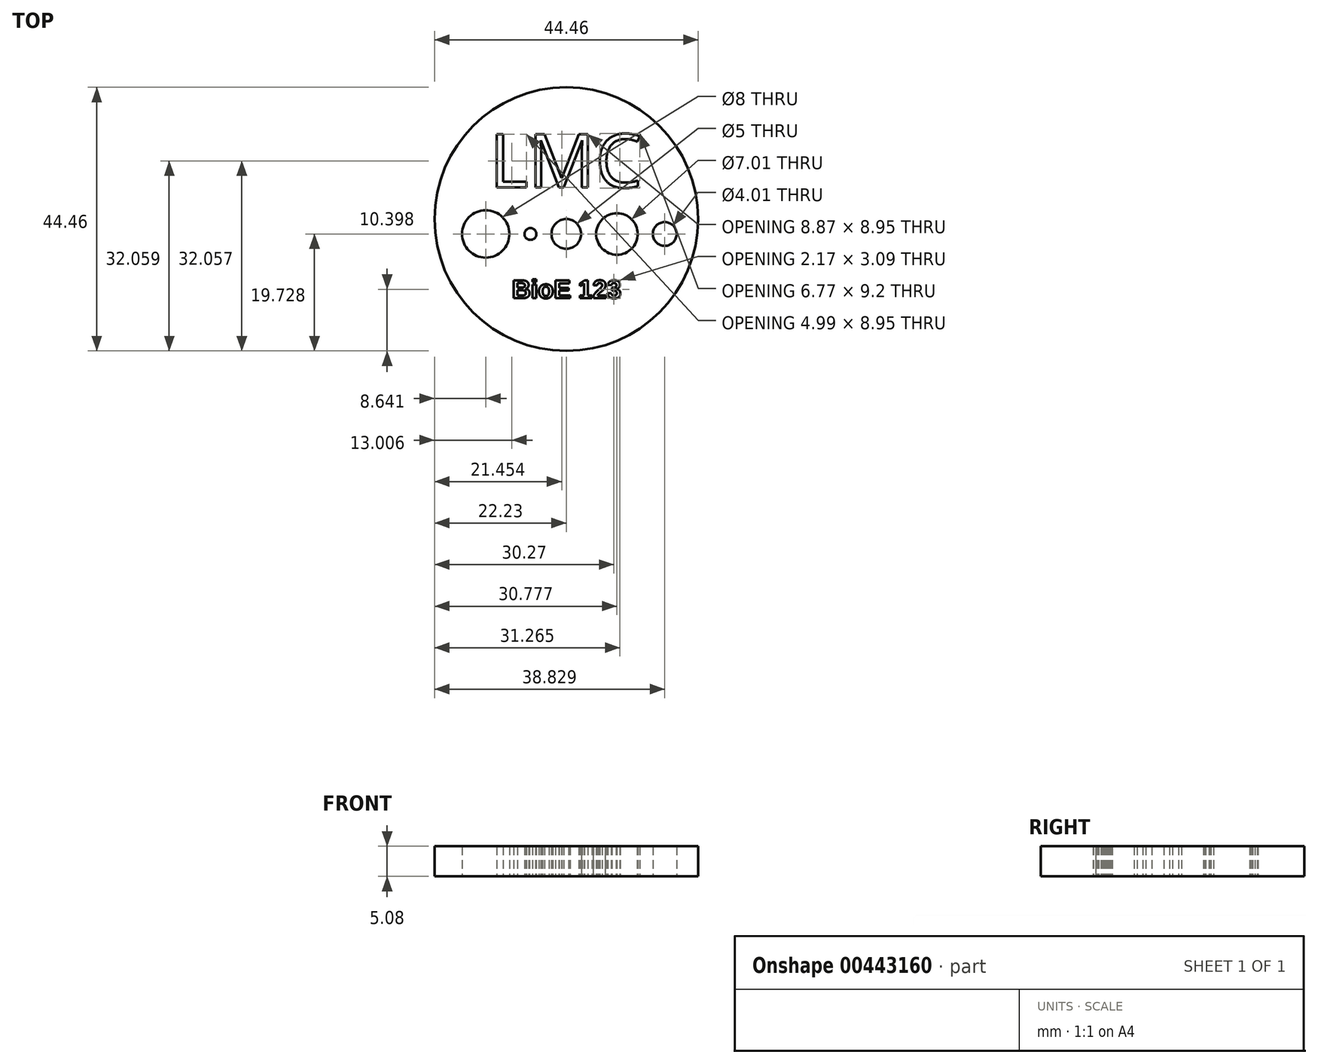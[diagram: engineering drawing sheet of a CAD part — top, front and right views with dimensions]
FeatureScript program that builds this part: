
annotation { "Feature Type Name" : "Feature", "Feature Type Description" : "" }
export const myFeature = defineFeature(function(context is Context, id is Id, definition is map)
    precondition{}
    {
        {
            var Q0;
            Q0=qCreatedBy(makeId("Top.planeOp"),FACE);
            var sketch = newSketch(context, id + "F0", { "sketchPlane" : qUnion([Q0])});
            skCircle(sketch, "E0", {"center": v(0, 0) * mm, "radius": 22.23 * mm});
            skSolve(sketch);
        }
        {
            var Q0;
            Q0=makeQuery(id+"F0.imprint","IMPRINT",FACE,{"disambiguationData":[TD([[makeQuery(id+"F0.imprint","IMPRINT",EDGE,{"derivedFrom":sQuery(id+"F0.wireOp",EDGE,"E0")}),1.0]])]});
            extrude(context, id + "F1", {"entities" : qUnion([Q0]), "depth" : 5.08 * mm});
        }
        {
            var Q0;
            Q0=qCreatedBy(makeId("Top.planeOp"),FACE);
            var sketch = newSketch(context, id + "F2", { "sketchPlane" : qUnion([Q0])});
            skCircle(sketch, "E1", {"center": v(-13.59, -2.5) * mm, "radius": 4 * mm});
            skCircle(sketch, "E2", {"center": v(-6.05, -2.5) * mm, "radius": 1 * mm});
            skCircle(sketch, "E3", {"center": v(0, -2.5) * mm, "radius": 2.5 * mm});
            skCircle(sketch, "E4", {"center": v(8.55, -2.5) * mm, "radius": 3.5 * mm});
            skCircle(sketch, "E5", {"center": v(16.6, -2.5) * mm, "radius": 2 * mm});
            skSolve(sketch);
        }
        {
            var Q0;
            Q0=qCreatedBy(makeId("Top.planeOp"),FACE);
            var sketch = newSketch(context, id + "F3", { "sketchPlane" : qUnion([Q0])});
            skText(sketch, "E6", { "text": "LMC", "fontName": "OpenSans-Regular.ttf"});
            const initialGuessF3  = {"E6": [-0.01295, 0.00535, 1, 0, 0.00903]};
            skSetInitialGuess(sketch, initialGuessF3);
            skSolve(sketch);
        }
        {
            var Q0;
            Q0=qCreatedBy(makeId("Top.planeOp"),FACE);
            var sketch = newSketch(context, id + "F4", { "sketchPlane" : qUnion([Q0])});
            skText(sketch, "E7", { "text": "BioE 123", "fontName": "Arimo-Bold.ttf"});
            const initialGuessF4  = {"E7": [-0.00914, -0.01333, 1, 0, 0.00314]};
            skSetInitialGuess(sketch, initialGuessF4);
            skSolve(sketch);
        }
        {
            var Q0;
            Q0 = qSketchRegion(id + "F2", true);
            var Q1;
            Q1 = qSketchRegion(id + "F3", true);
            var Q2;
            Q2 = qSketchRegion(id + "F4", true);
            extrude(context, id + "F5", {"entities" : qUnion([Q0, Q1, Q2]), "operationType" : NewBodyOperationType.REMOVE, "endBound" : BoundingType.THROUGH_ALL, "depth" : 25.4 * mm});
        }
    });
